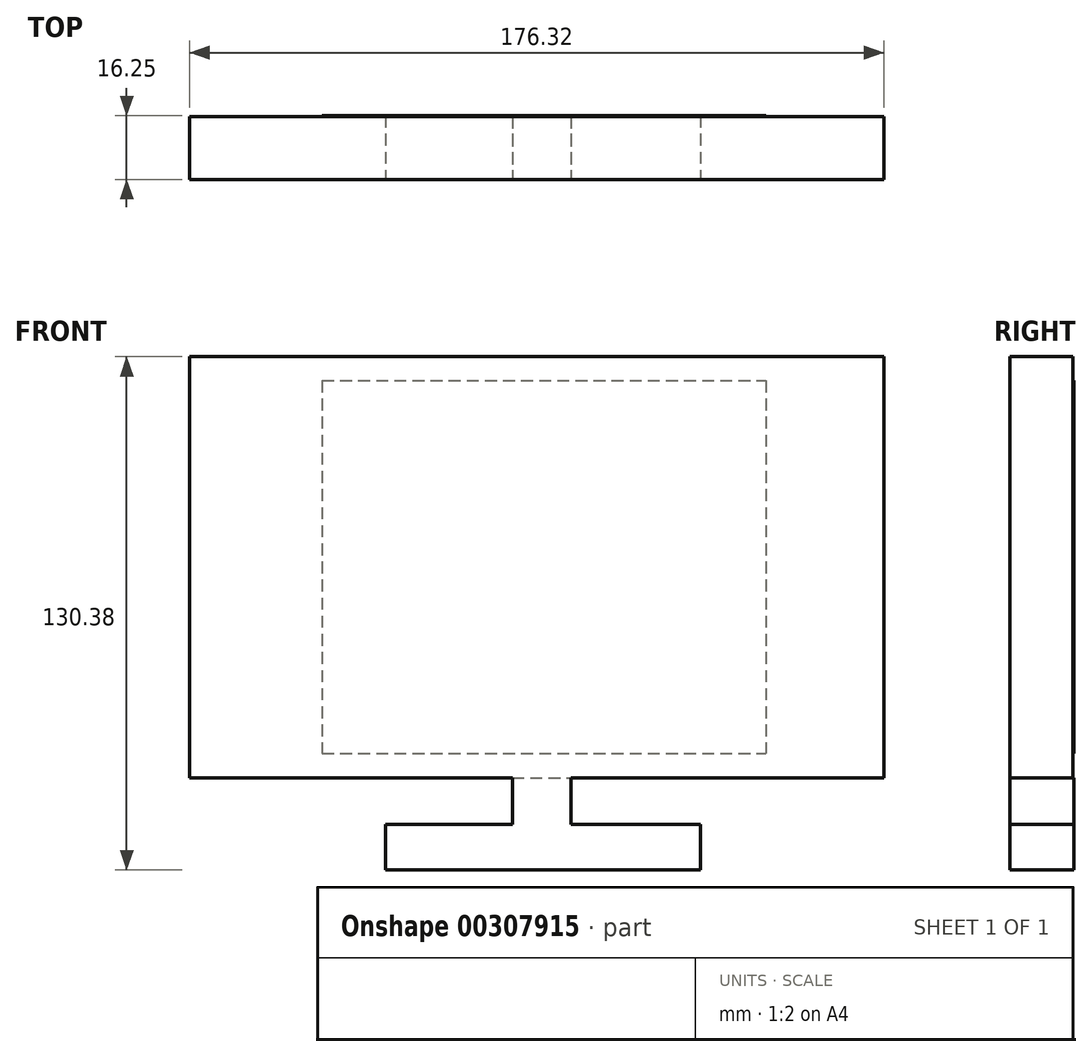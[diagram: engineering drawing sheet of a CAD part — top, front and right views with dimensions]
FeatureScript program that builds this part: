
annotation { "Feature Type Name" : "Feature", "Feature Type Description" : "" }
export const myFeature = defineFeature(function(context is Context, id is Id, definition is map)
    precondition{}
    {
        {
            var Q0;
            Q0=qCreatedBy(makeId("Front.planeOp"),FACE);
            var sketch = newSketch(context, id + "F0", { "sketchPlane" : qUnion([Q0])});
            skLineSegment(sketch, "E0", {"start": v(-89.72, 64.76) * mm, "end": v(-89.72, -42.3) * mm});
            skLineSegment(sketch, "E1", {"start": v(-89.72, -42.3) * mm, "end": v(86.6, -42.3) * mm});
            skLineSegment(sketch, "E2", {"start": v(86.6, -42.3) * mm, "end": v(86.6, 64.76) * mm});
            skLineSegment(sketch, "E3", {"start": v(86.6, 64.76) * mm, "end": v(-89.72, 64.76) * mm});
            skLineSegment(sketch, "E4", {"start": v(-85.16, 61.01) * mm, "end": v(-85.16, -39.14) * mm});
            skLineSegment(sketch, "E5", {"start": v(-85.16, -39.14) * mm, "end": v(82.8, -39.14) * mm});
            skLineSegment(sketch, "E6", {"start": v(82.8, -39.14) * mm, "end": v(82.8, 61.01) * mm});
            skLineSegment(sketch, "E7", {"start": v(82.8, 61.01) * mm, "end": v(-85.16, 61.01) * mm});
            skSolve(sketch);
        }
        {
            var Q0;
            Q0=makeQuery(id+"F0.imprint","IMPRINT",FACE,{"disambiguationData":[TD([[makeQuery(id+"F0.imprint","IMPRINT",EDGE,{"derivedFrom":sQuery(id+"F0.wireOp",EDGE,"E4")}),1.0]])]});
            var Q1;
            Q1=makeQuery(id+"F0.imprint","IMPRINT",FACE,{"disambiguationData":[TD([[makeQuery(id+"F0.imprint","IMPRINT",EDGE,{"derivedFrom":sQuery(id+"F0.wireOp",EDGE,"E0")}),1.0]])]});
            extrude(context, id + "F1", {"entities" : qUnion([Q0, Q1]), "depth" : 16 * mm});
        }
        {
            var Q0;
            Q0=makeQuery(id+"F1.opExtrude","CAP_FACE",FACE,{"disambiguationData":[OSD([sQuery(id+"F0.wireOp",EDGE,"E0"),sQuery(id+"F0.wireOp",EDGE,"E1"),sQuery(id+"F0.wireOp",EDGE,"E2"),sQuery(id+"F0.wireOp",EDGE,"E3")])],"isStart":false});
            var sketch = newSketch(context, id + "F2", { "sketchPlane" : qUnion([Q0])});
            skLineSegment(sketch, "E8", {"start": v(-7.77, -42.3) * mm, "end": v(-7.77, -54.1) * mm});
            skLineSegment(sketch, "E9", {"start": v(7.2, -42.3) * mm, "end": v(7.2, -54.1) * mm});
            skLineSegment(sketch, "E10", {"start": v(-40, -54.1) * mm, "end": v(40, -54.1) * mm});
            skLineSegment(sketch, "E11", {"start": v(40, -54.1) * mm, "end": v(40, -65.62) * mm});
            skLineSegment(sketch, "E12", {"start": v(-40, -54.1) * mm, "end": v(-40, -65.62) * mm});
            skLineSegment(sketch, "E13", {"start": v(-40, -65.62) * mm, "end": v(40, -65.62) * mm});
            skLineSegment(sketch, "E14.bottom", {"start": v(-56.12, 58.71) * mm, "end": v(56.7, 58.71) * mm});
            skLineSegment(sketch, "E14.top", {"start": v(-56.12, -35.98) * mm, "end": v(56.7, -35.98) * mm});
            skLineSegment(sketch, "E14.left", {"start": v(-56.12, 58.71) * mm, "end": v(-56.12, -35.98) * mm});
            skLineSegment(sketch, "E14.right", {"start": v(56.7, 58.71) * mm, "end": v(56.7, -35.98) * mm});
            skSolve(sketch);
        }
        {
            var Q0;
            {var subQ0=sQuery(id+"F2.wireOp",EDGE,"E11");Q0=makeQuery(id+"F2.imprint","IMPRINT",FACE,{"disambiguationData":[TD([[makeQuery(id+"F2.imprint","IMPRINT",EDGE,{"derivedFrom":subQ0}),-1.0]])]});}
            var Q1;
            {var subQ0=sQuery(id+"F2.wireOp",EDGE,"E8");Q1=makeQuery(id+"F2.imprint","IMPRINT",FACE,{"disambiguationData":[TD([[makeQuery(id+"F2.imprint","IMPRINT",EDGE,{"derivedFrom":subQ0}),1.0]])]});}
            var Q2;
            Q2=makeQuery(id+"F2.imprint","IMPRINT",FACE,{"disambiguationData":[TD([[makeQuery(id+"F2.imprint","IMPRINT",EDGE,{"derivedFrom":sQuery(id+"F2.wireOp",EDGE,"E14.bottom")}),-1.0]])]});
            extrude(context, id + "F3", {"entities" : qUnion([Q0, Q1, Q2]), "operationType" : NewBodyOperationType.ADD, "oppositeDirection" : true, "depth" : 16.26 * mm});
        }
    });
